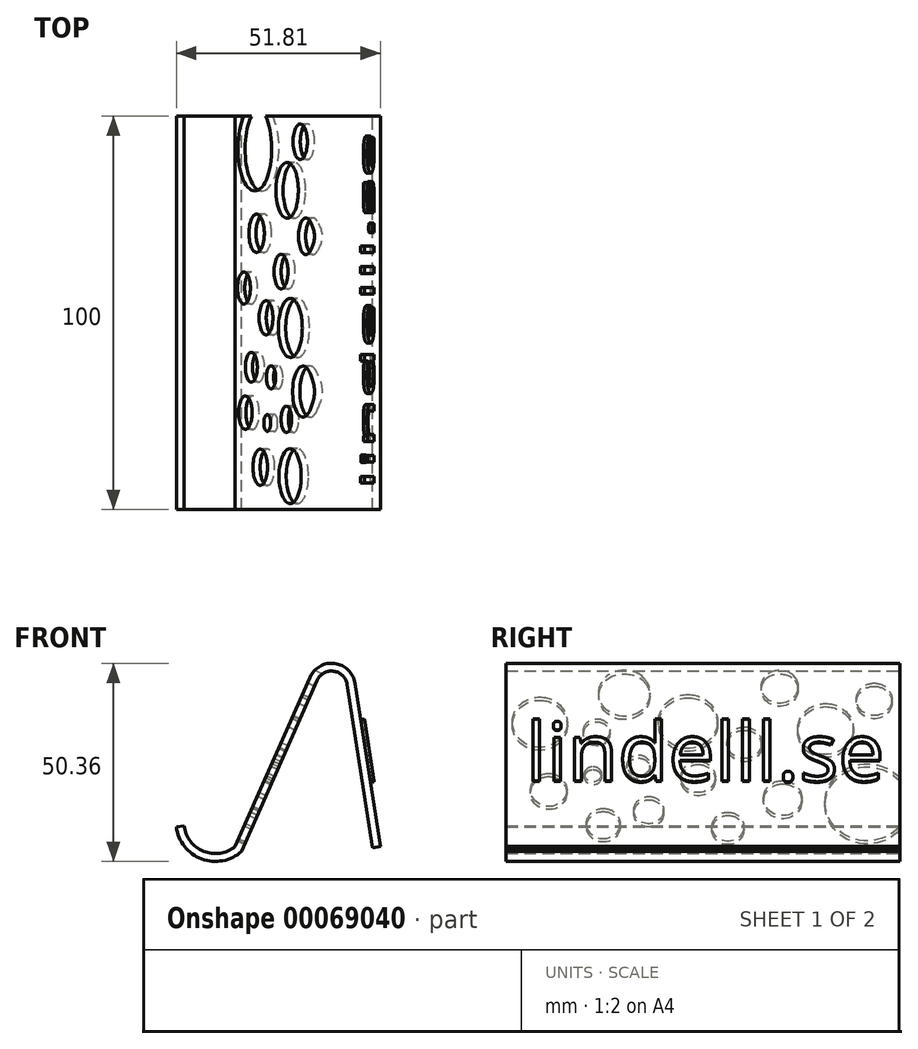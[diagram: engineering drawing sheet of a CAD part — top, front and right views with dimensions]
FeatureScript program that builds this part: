
annotation { "Feature Type Name" : "Feature", "Feature Type Description" : "" }
export const myFeature = defineFeature(function(context is Context, id is Id, definition is map)
    precondition{}
    {
        {
            var Q0;
            Q0=qCreatedBy(makeId("Front.planeOp"),FACE);
            var sketch = newSketch(context, id + "F0", { "sketchPlane" : qUnion([Q0])});
            skLineSegment(sketch, "E0", {"start": v(-27.24, 0) * mm, "end": v(-8.27, 43) * mm});
            skLineSegment(sketch, "E1", {"start": v(3.15, 41.5) * mm, "end": v(9.6, 0) * mm});
            skPoint(sketch, "E2.visualSharp", {"position": v(0, 61.74) * mm});
            skArc(sketch, "E2.filletArc", {"start": v(3.15, 41.5) * mm, "mid": v(-2, 46.53) * mm, "end": v(-8.27, 43) * mm});
            skArc(sketch, "E3", {"start": v(-40.22, 5.25) * mm, "mid": v(-35.28, -1.2) * mm, "end": v(-27.24, 0) * mm});
            skLineSegment(sketch, "E4.0", {"start": v(1.17, 41.2) * mm, "end": v(7.63, -0.3) * mm});
            skArc(sketch, "E4.1", {"start": v(1.17, 41.2) * mm, "mid": v(-2.26, 44.54) * mm, "end": v(-6.44, 42.2) * mm});
            skLineSegment(sketch, "E4.2", {"start": v(-25.6, -1.22) * mm, "end": v(-6.44, 42.2) * mm});
            skArc(sketch, "E4.3", {"start": v(-42.2, 5) * mm, "mid": v(-35.8, -3.15) * mm, "end": v(-25.6, -1.22) * mm});
            skLineSegment(sketch, "E5", {"start": v(-42.2, 5) * mm, "end": v(-40.22, 5.25) * mm});
            skLineSegment(sketch, "E6", {"start": v(7.63, -0.3) * mm, "end": v(9.6, 0) * mm});
            skSolve(sketch);
        }
        {
            var Q0;
            Q0=makeQuery(id+"F0.imprint","IMPRINT",FACE,{"disambiguationData":[TD([[makeQuery(id+"F0.imprint","IMPRINT",EDGE,{"derivedFrom":sQuery(id+"F0.wireOp",EDGE,"E0")}),-1.0]])]});
            extrude(context, id + "F1", {"entities" : qUnion([Q0]), "endBound" : BoundingType.SYMMETRIC, "depth" : 100 * mm});
        }
        {
            var Q0;
            Q0=makeQuery(id+"F1.opExtrude","SWEPT_FACE",FACE,{"disambiguationData":[OSD([sQuery(id+"F0.wireOp",EDGE,"E1")])]});
            var sketch = newSketch(context, id + "F2", { "sketchPlane" : qUnion([Q0])});
            skText(sketch, "E7", { "text": "lindelll.se", "fontName": "OpenSans-Regular.ttf"});
            const initialGuessF2  = {"E7": [-0.045, 0.01525, 1, 0, 0.01505]};
            skSetInitialGuess(sketch, initialGuessF2);
            skSolve(sketch);
        }
        {
            var Q0;
            Q0 = qSketchRegion(id + "F2", true);
            extrude(context, id + "F3", {"entities" : qUnion([Q0]), "operationType" : NewBodyOperationType.ADD, "depth" : 1 * mm});
        }
        {
            var Q0;
            Q0=makeQuery(id+"F1.opExtrude","SWEPT_FACE",FACE,{"disambiguationData":[OSD([sQuery(id+"F0.wireOp",EDGE,"E0")])]});
            var sketch = newSketch(context, id + "F4", { "sketchPlane" : qUnion([Q0])});
            skCircle(sketch, "E8", {"center": v(-43.48, 29.88) * mm, "radius": 4.5 * mm});
            skCircle(sketch, "E9", {"center": v(-31.12, 21.65) * mm, "radius": 7.08 * mm});
            skCircle(sketch, "E10", {"center": v(-41.68, 1.29) * mm, "radius": 10.69 * mm});
            skCircle(sketch, "E11", {"center": v(-10.5, 17.8) * mm, "radius": 4.4 * mm});
            skCircle(sketch, "E12", {"center": v(-20.23, 2.44) * mm, "radius": 4.87 * mm});
            skCircle(sketch, "E13", {"center": v(3.83, 23.7) * mm, "radius": 7.49 * mm});
            skCircle(sketch, "E14", {"center": v(-19.47, 33.43) * mm, "radius": 4.64 * mm});
            skCircle(sketch, "E15", {"center": v(1.24, 8.32) * mm, "radius": 4.35 * mm});
            skCircle(sketch, "E16", {"center": v(20, 31.6) * mm, "radius": 6.48 * mm});
            skCircle(sketch, "E17", {"center": v(16.36, 11.52) * mm, "radius": 2.93 * mm});
            skCircle(sketch, "E18", {"center": v(27.02, 21.17) * mm, "radius": 3.33 * mm});
            skCircle(sketch, "E19", {"center": v(39.22, 4.71) * mm, "radius": 4.6 * mm});
            skCircle(sketch, "E20", {"center": v(25.35, -4.65) * mm, "radius": 4.25 * mm});
            skCircle(sketch, "E21", {"center": v(13.8, -0.9) * mm, "radius": 3.79 * mm});
            skCircle(sketch, "E22", {"center": v(27.97, 9.1) * mm, "radius": 2.14 * mm});
            skCircle(sketch, "E23", {"center": v(41.49, 23.54) * mm, "radius": 6.99 * mm});
            skCircle(sketch, "E24", {"center": v(-6.31, -5.52) * mm, "radius": 4.04 * mm});
            skSolve(sketch);
        }
        {
            var Q0;
            Q0=makeQuery(id+"F4.imprint","IMPRINT",FACE,{"disambiguationData":[TD([[makeQuery(id+"F4.imprint","IMPRINT",EDGE,{"derivedFrom":sQuery(id+"F4.wireOp",EDGE,"E9")}),1.0]])]});
            var Q1;
            Q1=makeQuery(id+"F4.imprint","IMPRINT",FACE,{"disambiguationData":[TD([[makeQuery(id+"F4.imprint","IMPRINT",EDGE,{"derivedFrom":sQuery(id+"F4.wireOp",EDGE,"E8")}),1.0]])]});
            var Q2;
            {var subQ0=sQuery(id+"F4.wireOp",EDGE,"E10");var subQ1=makeQuery(id+"F1.opExtrude","CAP_EDGE",EDGE,{"disambiguationData":[OSD([sQuery(id+"F0.wireOp",EDGE,"E0")])],"isStart":true});var subQ2=makeQuery(id+"F4.imprint","INTERSECT",VERTEX,{"disambiguationData":[OD(0.0)],"derivedFrom":[subQ1,subQ0]});Q2=makeQuery(id+"F4.imprint","IMPRINT",FACE,{"disambiguationData":[TD([[makeQuery(id+"F4.imprint","IMPRINT",EDGE,{"disambiguationData":[TD([[subQ2,-1.0]])],"derivedFrom":subQ0}),1.0]])]});}
            var Q3;
            Q3=makeQuery(id+"F4.imprint","IMPRINT",FACE,{"disambiguationData":[TD([[makeQuery(id+"F4.imprint","IMPRINT",EDGE,{"derivedFrom":sQuery(id+"F4.wireOp",EDGE,"E12")}),1.0]])]});
            var Q4;
            Q4=makeQuery(id+"F4.imprint","IMPRINT",FACE,{"disambiguationData":[TD([[makeQuery(id+"F4.imprint","IMPRINT",EDGE,{"derivedFrom":sQuery(id+"F4.wireOp",EDGE,"E24")}),1.0]])]});
            var Q5;
            Q5=makeQuery(id+"F4.imprint","IMPRINT",FACE,{"disambiguationData":[TD([[makeQuery(id+"F4.imprint","IMPRINT",EDGE,{"derivedFrom":sQuery(id+"F4.wireOp",EDGE,"E11")}),1.0]])]});
            var Q6;
            {var subQ0=sQuery(id+"F4.wireOp",EDGE,"E14");var subQ1=makeQuery(id+"F1.opExtrude","SWEPT_EDGE",EDGE,{"disambiguationData":[OSD([sQuery(id+"F0.wireOp",EDGE,"E0"),sQuery(id+"F0.wireOp",EDGE,"E2.filletArc")])]});var subQ2=makeQuery(id+"F4.imprint","INTERSECT",VERTEX,{"disambiguationData":[OD(0.0)],"derivedFrom":[subQ1,subQ0]});Q6=makeQuery(id+"F4.imprint","IMPRINT",FACE,{"disambiguationData":[TD([[makeQuery(id+"F4.imprint","IMPRINT",EDGE,{"disambiguationData":[TD([[subQ2,-1.0]])],"derivedFrom":subQ0}),1.0]])]});}
            var Q7;
            Q7=makeQuery(id+"F4.imprint","IMPRINT",FACE,{"disambiguationData":[TD([[makeQuery(id+"F4.imprint","IMPRINT",EDGE,{"derivedFrom":sQuery(id+"F4.wireOp",EDGE,"E13")}),1.0]])]});
            var Q8;
            Q8=makeQuery(id+"F4.imprint","IMPRINT",FACE,{"disambiguationData":[TD([[makeQuery(id+"F4.imprint","IMPRINT",EDGE,{"derivedFrom":sQuery(id+"F4.wireOp",EDGE,"E15")}),1.0]])]});
            var Q9;
            Q9=makeQuery(id+"F4.imprint","IMPRINT",FACE,{"disambiguationData":[TD([[makeQuery(id+"F4.imprint","IMPRINT",EDGE,{"derivedFrom":sQuery(id+"F4.wireOp",EDGE,"E21")}),1.0]])]});
            var Q10;
            Q10=makeQuery(id+"F4.imprint","IMPRINT",FACE,{"disambiguationData":[TD([[makeQuery(id+"F4.imprint","IMPRINT",EDGE,{"derivedFrom":sQuery(id+"F4.wireOp",EDGE,"E20")}),1.0]])]});
            var Q11;
            Q11=makeQuery(id+"F4.imprint","IMPRINT",FACE,{"disambiguationData":[TD([[makeQuery(id+"F4.imprint","IMPRINT",EDGE,{"derivedFrom":sQuery(id+"F4.wireOp",EDGE,"E17")}),1.0]])]});
            var Q12;
            Q12=makeQuery(id+"F4.imprint","IMPRINT",FACE,{"disambiguationData":[TD([[makeQuery(id+"F4.imprint","IMPRINT",EDGE,{"derivedFrom":sQuery(id+"F4.wireOp",EDGE,"E22")}),1.0]])]});
            var Q13;
            Q13=makeQuery(id+"F4.imprint","IMPRINT",FACE,{"disambiguationData":[TD([[makeQuery(id+"F4.imprint","IMPRINT",EDGE,{"derivedFrom":sQuery(id+"F4.wireOp",EDGE,"E19")}),1.0]])]});
            var Q14;
            Q14=makeQuery(id+"F4.imprint","IMPRINT",FACE,{"disambiguationData":[TD([[makeQuery(id+"F4.imprint","IMPRINT",EDGE,{"derivedFrom":sQuery(id+"F4.wireOp",EDGE,"E23")}),1.0]])]});
            var Q15;
            Q15=makeQuery(id+"F4.imprint","IMPRINT",FACE,{"disambiguationData":[TD([[makeQuery(id+"F4.imprint","IMPRINT",EDGE,{"derivedFrom":sQuery(id+"F4.wireOp",EDGE,"E18")}),1.0]])]});
            var Q16;
            {var subQ0=sQuery(id+"F4.wireOp",EDGE,"E16");var subQ1=makeQuery(id+"F1.opExtrude","SWEPT_EDGE",EDGE,{"disambiguationData":[OSD([sQuery(id+"F0.wireOp",EDGE,"E0"),sQuery(id+"F0.wireOp",EDGE,"E2.filletArc")])]});var subQ2=makeQuery(id+"F4.imprint","INTERSECT",VERTEX,{"disambiguationData":[OD(0.0)],"derivedFrom":[subQ1,subQ0]});Q16=makeQuery(id+"F4.imprint","IMPRINT",FACE,{"disambiguationData":[TD([[makeQuery(id+"F4.imprint","IMPRINT",EDGE,{"disambiguationData":[TD([[subQ2,1.0]])],"derivedFrom":subQ0}),1.0]])]});}
            var Q17;
            {var subQ0=sQuery(id+"F4.wireOp",EDGE,"E16");var subQ1=makeQuery(id+"F1.opExtrude","SWEPT_EDGE",EDGE,{"disambiguationData":[OSD([sQuery(id+"F0.wireOp",EDGE,"E0"),sQuery(id+"F0.wireOp",EDGE,"E2.filletArc")])]});var subQ2=makeQuery(id+"F4.imprint","INTERSECT",VERTEX,{"disambiguationData":[OD(0.0)],"derivedFrom":[subQ1,subQ0]});Q17=makeQuery(id+"F4.imprint","IMPRINT",FACE,{"disambiguationData":[TD([[makeQuery(id+"F4.imprint","IMPRINT",EDGE,{"disambiguationData":[TD([[subQ2,-1.0]])],"derivedFrom":subQ0}),1.0]])]});}
            var Q18;
            {var subQ0=sQuery(id+"F4.wireOp",EDGE,"E14");var subQ1=makeQuery(id+"F1.opExtrude","SWEPT_EDGE",EDGE,{"disambiguationData":[OSD([sQuery(id+"F0.wireOp",EDGE,"E0"),sQuery(id+"F0.wireOp",EDGE,"E2.filletArc")])]});var subQ2=makeQuery(id+"F4.imprint","INTERSECT",VERTEX,{"disambiguationData":[OD(0.0)],"derivedFrom":[subQ1,subQ0]});Q18=makeQuery(id+"F4.imprint","IMPRINT",FACE,{"disambiguationData":[TD([[makeQuery(id+"F4.imprint","IMPRINT",EDGE,{"disambiguationData":[TD([[subQ2,1.0]])],"derivedFrom":subQ0}),1.0]])]});}
            extrude(context, id + "F5", {"entities" : qUnion([Q0, Q1, Q2, Q3, Q4, Q5, Q6, Q7, Q8, Q9, Q10, Q11, Q12, Q13, Q14, Q15, Q16, Q17, Q18]), "operationType" : NewBodyOperationType.REMOVE, "endBound" : BoundingType.UP_TO_NEXT, "oppositeDirection" : true, "depth" : 3 * mm});
        }
    });
